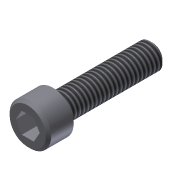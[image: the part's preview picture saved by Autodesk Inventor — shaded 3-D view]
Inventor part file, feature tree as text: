
AUTODESK INVENTOR PART (.ipt)
format: ipt  version: 2011 SP1 (Build 150282100, 282)  size: 106,496 bytes
history: native  units: in
note: dims shown in document units (in); Inventor stores cm internally (conversion verified against a paired STEP export)
features: extrude x3, sketch x3, chamfer x2, thread x1
ambient origin geometry x8: Origin, YZ Plane, XZ Plane, XY Plane, X Axis, Y Axis, Z Axis, Center Point
bodies: Solid1 (feature_tree)
feature tree (9):
  extrude  "Extrusion1"  Depth=0.19in TaperAngle=0.0deg
  extrude  "Extrusion2"  Depth=0.75in TaperAngle=0.0deg
  extrude  "Extrusion3"  Depth=0.125in TaperAngle=0.0deg
  thread  "Thread1"  [1 undecoded]
  chamfer  "Chamfer1"  Distance=0.02in Angle=45.0deg
  chamfer  "Chamfer2"  Distance=0.02in Angle=45.0deg
  sketch  "Sketch1"  dims[d0=0.312in d1=0.19in d2=0.0in]
  sketch  "Sketch2"  dims[d3=0.19in d4=0.75in d5=0.0in]
  sketch  "Sketch3"  dims[d6=0.1562in d7=0.125in d8=0.0in d9=1.0in d10=0.0in d11=0.02in d12=0.125in d13=45.0deg d14=0.02in d15=0.125in d16=45.0deg]
note: 1 required parameter value undecoded (feature->parameter linkage not recoverable at this tier; creation-order binding heuristic only, values carry confidence <= 0.55)
